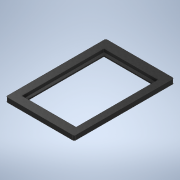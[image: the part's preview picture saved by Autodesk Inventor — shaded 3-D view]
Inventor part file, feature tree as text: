
AUTODESK INVENTOR PART (.ipt)
format: ipt  version: 2020 (Build 240168000, 168)  size: 142,848 bytes
history: native  units: mm
features: extrude x2, sketch x2, fillet x1
ambient origin geometry x8: Origin, YZ Plane, XZ Plane, XY Plane, X Axis, Y Axis, Z Axis, Center Point
bodies: 实体1 (feature_tree)
feature tree (5):
  extrude  "拉伸1"  Depth=108.0mm
  fillet  "圆角1"  Radius=43.0mm
  extrude  "拉伸2"  Depth=86.0mm
  sketch  "草图1"  dims[d0=158.0mm d1=108.0mm d2=43.0mm]
  sketch  "草图2"  dims[d4=65.0mm d5=86.0mm d6=130.0mm d7=7.2mm d8=0.0mm d9=2.0mm d10=4.0mm d11=4.0mm d12=78.0mm d13=122.0mm d14=2.0mm d15=0.0mm]
